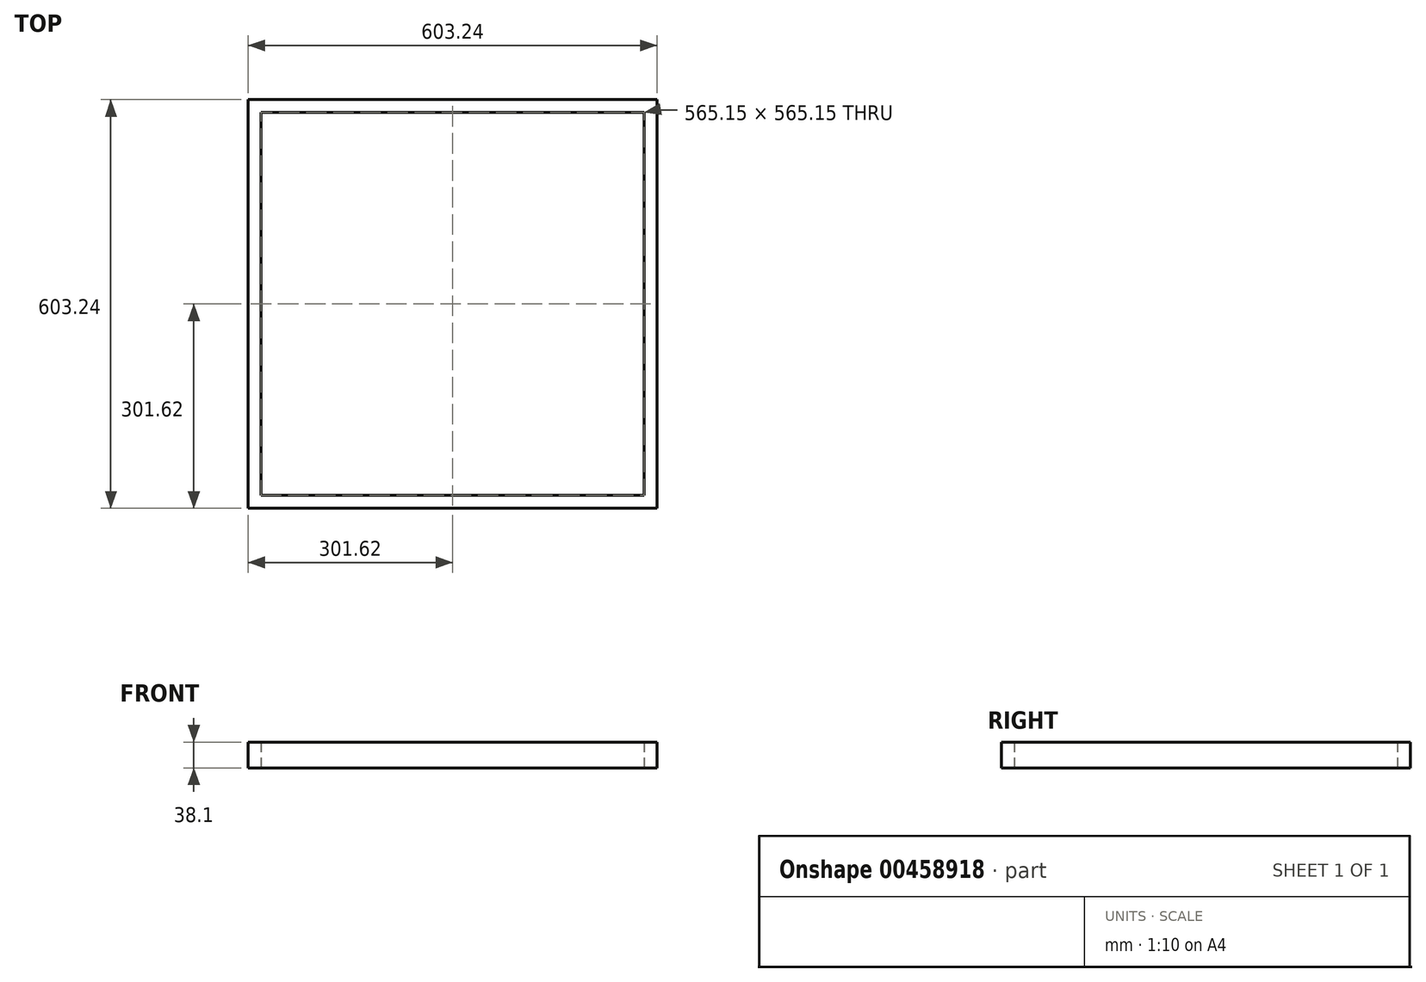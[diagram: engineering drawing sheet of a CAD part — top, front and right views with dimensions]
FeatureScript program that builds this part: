
annotation { "Feature Type Name" : "Feature", "Feature Type Description" : "" }
export const myFeature = defineFeature(function(context is Context, id is Id, definition is map)
    precondition{}
    {
        {
            var Q0;
            Q0=qCreatedBy(makeId("Top.planeOp"),FACE);
            var sketch = newSketch(context, id + "F0", { "sketchPlane" : qUnion([Q0])});
            skLineSegment(sketch, "E0.bottom", {"start": v(-301.62, 301.63) * mm, "end": v(301.63, 301.63) * mm});
            skLineSegment(sketch, "E0.top", {"start": v(-301.63, -301.63) * mm, "end": v(301.63, -301.63) * mm});
            skLineSegment(sketch, "E0.left", {"start": v(-301.62, 301.63) * mm, "end": v(-301.63, -301.62) * mm});
            skLineSegment(sketch, "E0.right", {"start": v(301.63, 301.63) * mm, "end": v(301.62, -301.62) * mm});
            skLineSegment(sketch, "E1", {"start": v(-301.62, 301.63) * mm, "end": v(301.63, -301.63) * mm, "construction": true});
            skLineSegment(sketch, "E2.bottom", {"start": v(-282.57, 282.58) * mm, "end": v(282.57, 282.58) * mm});
            skLineSegment(sketch, "E2.top", {"start": v(-282.57, -282.57) * mm, "end": v(282.57, -282.57) * mm});
            skLineSegment(sketch, "E2.left", {"start": v(-282.57, 282.58) * mm, "end": v(-282.57, -282.57) * mm});
            skLineSegment(sketch, "E2.right", {"start": v(282.57, 282.58) * mm, "end": v(282.57, -282.57) * mm});
            skSolve(sketch);
        }
        {
            var Q0;
            Q0=makeQuery(id+"F0.imprint","IMPRINT",FACE,{"disambiguationData":[TD([[makeQuery(id+"F0.imprint","IMPRINT",EDGE,{"derivedFrom":sQuery(id+"F0.wireOp",EDGE,"E0.bottom")}),-1.0]])]});
            extrude(context, id + "F1", {"entities" : qUnion([Q0]), "depth" : 38.1 * mm});
        }
    });
